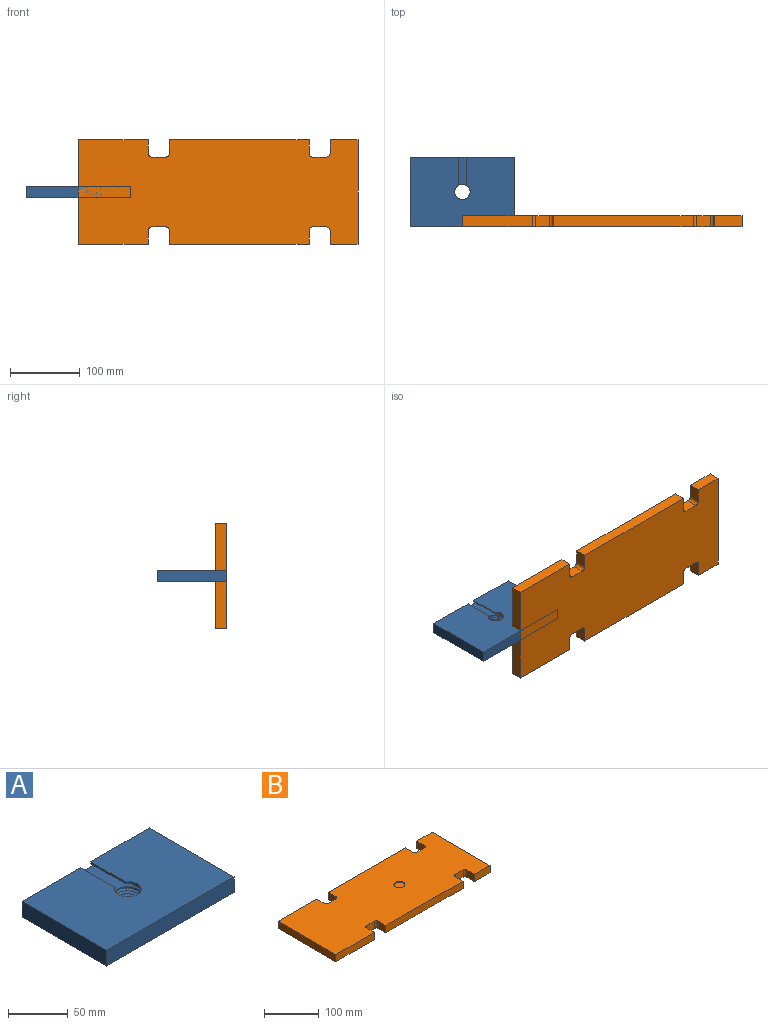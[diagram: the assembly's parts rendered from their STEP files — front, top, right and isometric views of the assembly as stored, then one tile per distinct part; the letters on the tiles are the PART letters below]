
ASSEMBLY  parts=2 mates=1
PART A: 18 faces, bbox 150x100x17.9 mm
  f0: cylinder r=11mm len=22mm, axis (0,0,1), area 120.4mm2, adj f10,f11,f15,f16,f17
  f1: cylinder r=12.5mm len=25mm, axis (0,0,-1), area 117.8mm2, adj f11,f12,f13,f14
  f2: plane 40.78x2mm, normal (1,0,0), area 81.6mm2, adj f4,f5,f7,f12
  f3: plane 40.78x2mm, normal (-1,0,0), area 81.6mm2, adj f4,f5,f7,f12
  f4: plane 150x100mm, normal (0,0,1), area 14145mm2, adj f2,f3,f5,f6,f7,f8,f9
  f5: cylinder r=11mm len=22mm, axis (0,0,1), area 112.8mm2, adj f2,f3,f4,f12
  f6: plane 100x16mm, normal (1,0,0), area 1600mm2, adj f4,f7,f9,f10
  f7: plane 150x16mm, normal (0,1,0), area 2301mm2, adj f2,f3,f4,f6,f8,f10,f11,f12
  f8: plane 100x16mm, normal (-1,0,0), area 1600mm2, adj f4,f7,f9,f10
  f9: plane 150x16mm, normal (0,-1,0), area 2400mm2, adj f4,f6,f8,f10
  f10: plane 150x100mm, normal (0,0,-1), area 14529.2mm2, adj f0,f6,f7,f8,f9,f15,f16
  f11: plane 62.5x25mm, normal (0,0,1), area 1115.3mm2, adj f0,f1,f7,f13,f14
  f12: plane 62.5x25mm, normal (0,0,-1), area 640.4mm2, adj f1,f2,f3,f5,f7,f13,f14
  f13: plane 50x3mm, normal (1,0,0), area 150mm2, adj f1,f7,f11,f12
  f14: plane 50x3mm, normal (-1,0,0), area 150mm2, adj f1,f7,f11,f12
  f15: bspline ~31.2x27.02mm, area 763.1mm2, adj f0,f10,f16,f17
  f16: bspline ~31.2x27.02mm, area 659.3mm2, adj f0,f10,f15,f17
  f17: plane 2.9x2.18mm, normal (-0.87,0.5,0), area 3.6mm2, adj f0,f15,f16
PART B: 32 faces, bbox 400x150x16 mm
  f0: plane 100x16mm, normal (0,1,0), area 1600mm2, adj f6,f8,f9,f13
  f1: plane 200x16mm, normal (0,1,0), area 3200mm2, adj f8,f9,f10,f15
  f2: plane 200x16mm, normal (0,-1,0), area 3200mm2, adj f8,f9,f18,f20
  f3: plane 100x16mm, normal (0,-1,0), area 1600mm2, adj f6,f8,f9,f17
  f4: plane 150x16mm, normal (1,0,0), area 2400mm2, adj f5,f7,f8,f9
  f5: plane 40x16mm, normal (0,1,0), area 640mm2, adj f4,f8,f9,f12
  f6: plane 150x16mm, normal (-1,0,0), area 2400mm2, adj f0,f3,f8,f9
  f7: plane 40x16mm, normal (0,-1,0), area 640mm2, adj f4,f8,f9,f21
  f8: plane 400x150mm, normal (0,0,1), area 56728.8mm2, adj f0,f1,f2,f3,f4,f5,f6,f7
  f9: plane 400x150mm, normal (0,0,-1), area 57042.9mm2, adj f0,f1,f2,f3,f4,f5,f6,f7
  f10: plane 20x16mm, normal (1,0,0), area 320mm2, adj f1,f8,f9,f29
  f11: plane 20x16mm, normal (0,1,0), area 320mm2, adj f8,f9,f28,f29
  f12: plane 20x16mm, normal (-1,0,0), area 320mm2, adj f5,f8,f9,f28
  f13: plane 20x16mm, normal (1,0,0), area 320mm2, adj f0,f8,f9,f26
  f14: plane 20x16mm, normal (0,1,0), area 320mm2, adj f8,f9,f26,f27
  f15: plane 20x16mm, normal (-1,0,0), area 320mm2, adj f1,f8,f9,f27
  f16: plane 20x16mm, normal (0,-1,0), area 320mm2, adj f8,f9,f24,f25
  f17: plane 20x16mm, normal (1,0,0), area 320mm2, adj f3,f8,f9,f25
  f18: plane 20x16mm, normal (-1,0,0), area 320mm2, adj f2,f8,f9,f24
  f19: plane 20x16mm, normal (0,-1,0), area 320mm2, adj f8,f9,f22,f23
  f20: plane 20x16mm, normal (1,0,0), area 320mm2, adj f2,f8,f9,f23
  f21: plane 20x16mm, normal (-1,0,0), area 320mm2, adj f7,f8,f9,f22
  f22: cylinder r=5mm len=16mm, axis (0,0,-1), area 125.7mm2, adj f8,f9,f19,f21
  f23: cylinder r=5mm len=16mm, axis (0,0,1), area 125.7mm2, adj f8,f9,f19,f20
  f24: cylinder r=5mm len=16mm, axis (0,0,-1), area 125.7mm2, adj f8,f9,f16,f18
  f25: cylinder r=5mm len=16mm, axis (0,0,1), area 125.7mm2, adj f8,f9,f16,f17
  f26: cylinder r=5mm len=16mm, axis (0,0,-1), area 125.7mm2, adj f8,f9,f13,f14
  f27: cylinder r=5mm len=16mm, axis (0,0,1), area 125.7mm2, adj f8,f9,f14,f15
  f28: cylinder r=5mm len=16mm, axis (0,0,1), area 125.7mm2, adj f8,f9,f11,f12
  f29: cylinder r=5mm len=16mm, axis (0,0,-1), area 125.7mm2, adj f8,f9,f10,f11
  f30: cylinder r=10mm len=20mm, axis (0,0,1), area 125.7mm2, adj f8,f31
  f31: plane 20x20mm, normal (0,0,1), area 314.2mm2, adj f30
PLACE A at identity
PLACE B rot(axis=(-1,0,0),90deg) t=(200,-50,8)mm
MATE planar B.f9 <-> A.f9  axis (0,-1,0) through (0,-50,8)mm
